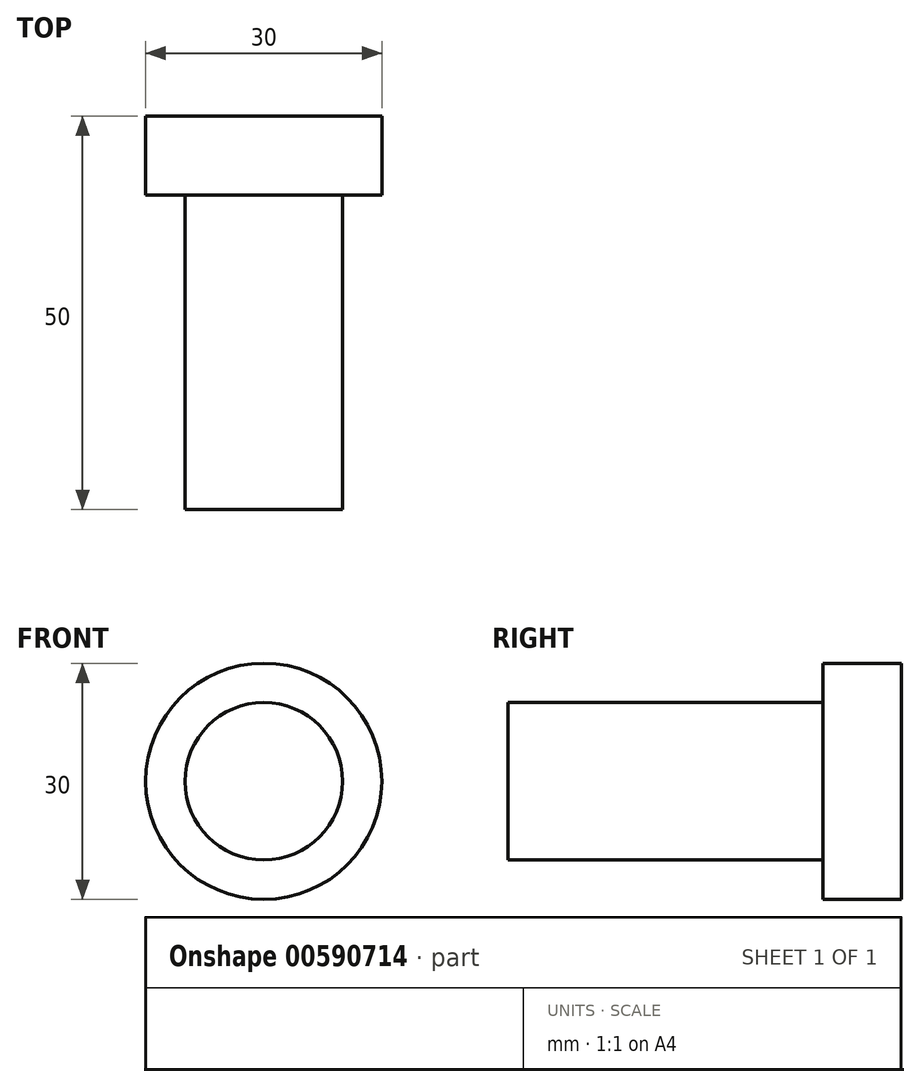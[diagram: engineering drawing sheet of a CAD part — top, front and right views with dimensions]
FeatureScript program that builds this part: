
annotation { "Feature Type Name" : "Feature", "Feature Type Description" : "" }
export const myFeature = defineFeature(function(context is Context, id is Id, definition is map)
    precondition{}
    {
        {
            var Q0;
            Q0=qCreatedBy(makeId("Front.planeOp"),FACE);
            var sketch = newSketch(context, id + "F0", { "sketchPlane" : qUnion([Q0])});
            skCircle(sketch, "E0", {"center": v(0, 0) * mm, "radius": 10 * mm});
            skCircle(sketch, "E1", {"center": v(0, 0) * mm, "radius": 15 * mm});
            skSolve(sketch);
        }
        {
            var Q0;
            Q0=makeQuery(id+"F0.imprint","IMPRINT",FACE,{"disambiguationData":[TD([[makeQuery(id+"F0.imprint","IMPRINT",EDGE,{"derivedFrom":sQuery(id+"F0.wireOp",EDGE,"E0")}),1.0]])]});
            extrude(context, id + "F1", {"entities" : qUnion([Q0]), "depth" : 40 * mm, "offsetDistance" : 25 * mm});
        }
        {
            var Q0;
            Q0 = qSketchRegion(id + "FC0n7TtWh5OLf7t_1", true);
            var Q1;
            Q1=makeQuery(id+"F0.imprint","IMPRINT",FACE,{"disambiguationData":[TD([[makeQuery(id+"F0.imprint","IMPRINT",EDGE,{"derivedFrom":sQuery(id+"F0.wireOp",EDGE,"E0")}),1.0]])]});
            var Q2;
            Q2=makeQuery(id+"F0.imprint","IMPRINT",FACE,{"disambiguationData":[TD([[makeQuery(id+"F0.imprint","IMPRINT",EDGE,{"derivedFrom":sQuery(id+"F0.wireOp",EDGE,"E0")}),-1.0]])]});
            extrude(context, id + "F2", {"entities" : qUnion([Q0, Q1, Q2]), "operationType" : NewBodyOperationType.ADD, "oppositeDirection" : true, "depth" : 10 * mm, "offsetDistance" : 25 * mm});
        }
    });
